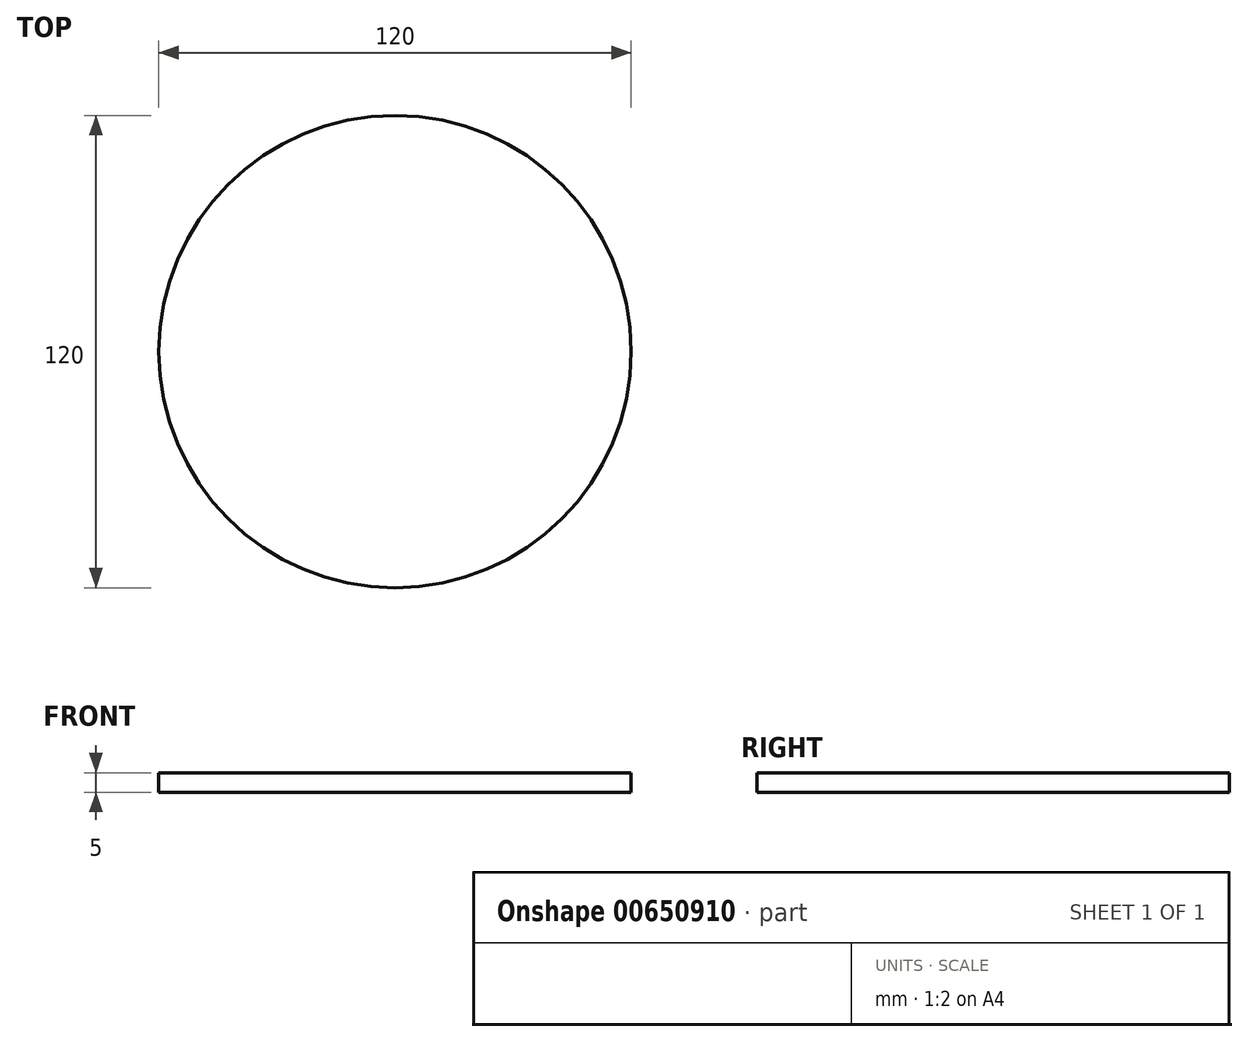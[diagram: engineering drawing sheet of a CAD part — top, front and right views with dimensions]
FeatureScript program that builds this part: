
annotation { "Feature Type Name" : "Feature", "Feature Type Description" : "" }
export const myFeature = defineFeature(function(context is Context, id is Id, definition is map)
    precondition{}
    {
        {
            var Q0;
            Q0=qCreatedBy(makeId("Top.planeOp"),FACE);
            var sketch = newSketch(context, id + "F0", { "sketchPlane" : qUnion([Q0])});
            skCircle(sketch, "E0", {"center": v(0, 0) * mm, "radius": 60 * mm});
            skLineSegment(sketch, "E1", {"start": v(0, 0) * mm, "end": v(60, 0) * mm});
            skSolve(sketch);
        }
        {
            var Q0;
            Q0 = qSketchRegion(id + "F0", true);
            extrude(context, id + "F1", {"entities" : qUnion([Q0]), "depth" : 5 * mm, "offsetDistance" : 25 * mm});
        }
    });
